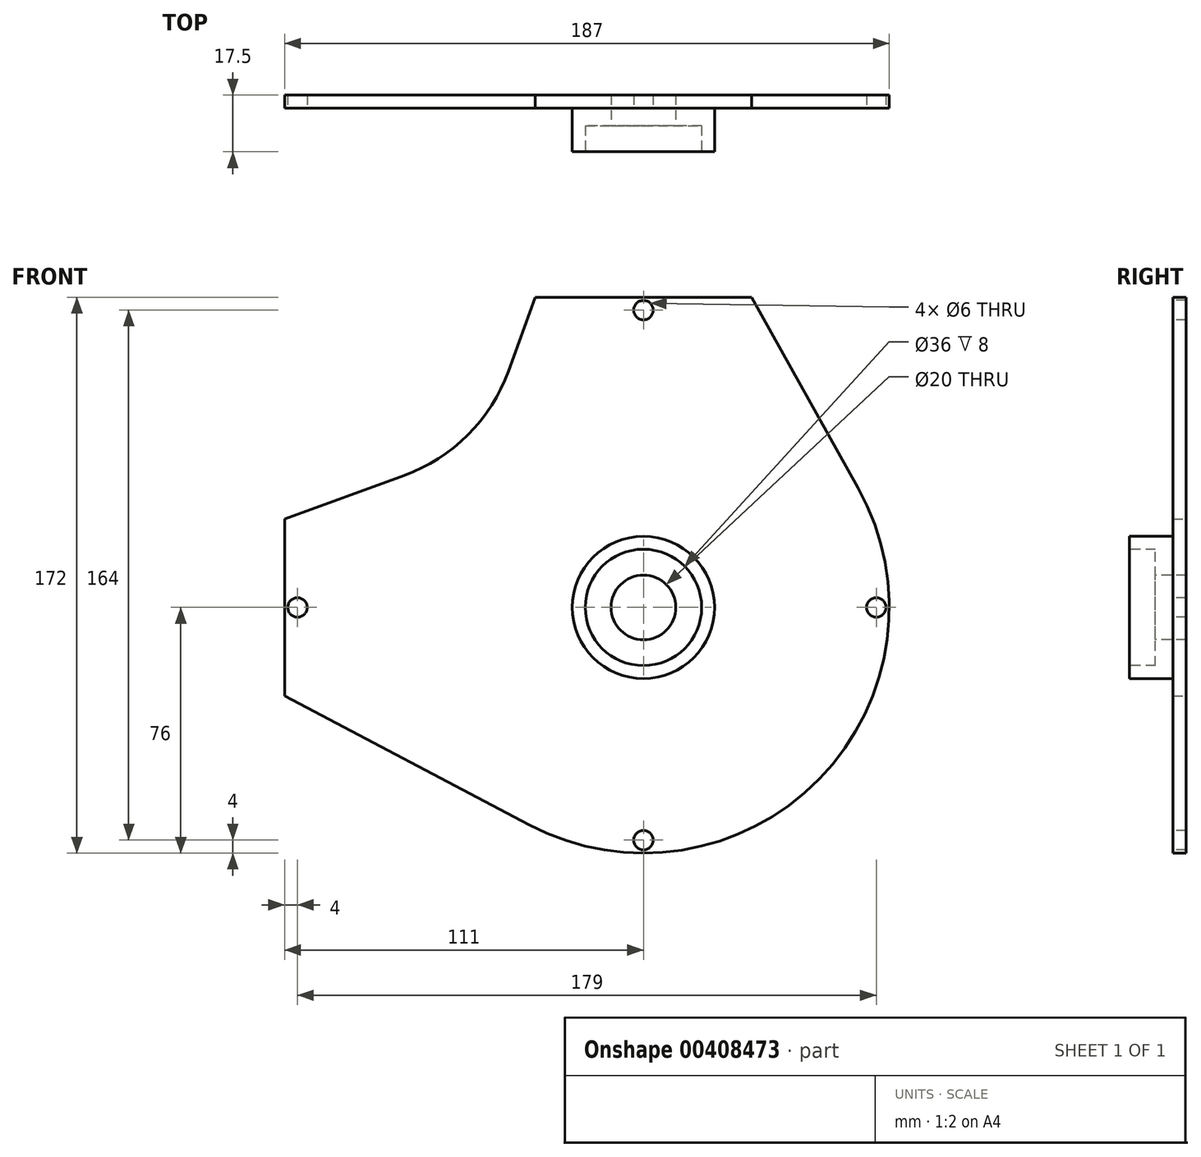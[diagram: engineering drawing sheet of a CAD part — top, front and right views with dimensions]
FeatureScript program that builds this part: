
annotation { "Feature Type Name" : "Feature", "Feature Type Description" : "" }
export const myFeature = defineFeature(function(context is Context, id is Id, definition is map)
    precondition{}
    {
        {
            var Q0;
            Q0=qCreatedBy(makeId("Front.planeOp"),FACE);
            var sketch = newSketch(context, id + "F0", { "sketchPlane" : qUnion([Q0])});
            skLineSegment(sketch, "E0", {"start": v(-33.42, 96) * mm, "end": v(33.42, 96) * mm});
            skLineSegment(sketch, "E1", {"start": v(-111, 27.4) * mm, "end": v(-111, -27.4) * mm});
            skArc(sketch, "E2", {"start": v(66.35, 37.07) * mm, "mid": v(54.39, -53.08) * mm, "end": v(-35.45, -67.23) * mm});
            skLineSegment(sketch, "E3", {"start": v(-111, -27.39) * mm, "end": v(-35.45, -67.23) * mm});
            skLineSegment(sketch, "E4", {"start": v(33.42, 96) * mm, "end": v(66.35, 37.07) * mm});
            skLineSegment(sketch, "E5", {"start": v(-33.42, 96) * mm, "end": v(-41.75, 73.12) * mm});
            skLineSegment(sketch, "E6", {"start": v(-111, 27.39) * mm, "end": v(-74.02, 40.85) * mm});
            skArc(sketch, "E7", {"start": v(-41.75, 73.12) * mm, "mid": v(-54.3, 53.4) * mm, "end": v(-74.02, 40.85) * mm});
            skSolve(sketch);
        }
        {
            var Q0;
            Q0=makeQuery(id+"F0.imprint","IMPRINT",FACE,{"disambiguationData":[TD([[makeQuery(id+"F0.imprint","IMPRINT",EDGE,{"derivedFrom":sQuery(id+"F0.wireOp",EDGE,"E0")}),-1.0]])]});
            extrude(context, id + "F1", {"entities" : qUnion([Q0]), "depth" : 4 * mm});
        }
        {
            var Q0;
            Q0=makeQuery(id+"F1.opExtrude","CAP_FACE",FACE,{"disambiguationData":[OSD([sQuery(id+"F0.wireOp",EDGE,"E0"),sQuery(id+"F0.wireOp",EDGE,"E1"),sQuery(id+"F0.wireOp",EDGE,"E2"),sQuery(id+"F0.wireOp",EDGE,"E3"),sQuery(id+"F0.wireOp",EDGE,"E4"),sQuery(id+"F0.wireOp",EDGE,"E5"),sQuery(id+"F0.wireOp",EDGE,"E6"),sQuery(id+"F0.wireOp",EDGE,"E7")])],"isStart":false});
            var sketch = newSketch(context, id + "F2", { "sketchPlane" : qUnion([Q0])});
            skPoint(sketch, "E8", {"position": v(0, 92) * mm});
            skPoint(sketch, "E9", {"position": v(-107, 0) * mm});
            skPoint(sketch, "E10", {"position": v(0, -72) * mm});
            skPoint(sketch, "E11", {"position": v(72, 0) * mm});
            skSolve(sketch);
        }
        {
            var Q0;
            Q0=sQuery(id+"F2.wireOp",VERTEX,"E8");
            var Q1;
            Q1=sQuery(id+"F2.wireOp",VERTEX,"E9");
            var Q2;
            Q2=sQuery(id+"F2.wireOp",VERTEX,"E10");
            var Q3;
            Q3=sQuery(id+"F2.wireOp",VERTEX,"E11");
            var Q4;
            Q4=makeQuery(id+"F1.opExtrude","SWEPT_BODY",BODY,{"disambiguationData":[OSD([sQuery(id+"F0.wireOp",EDGE,"E0"),sQuery(id+"F0.wireOp",EDGE,"E1"),sQuery(id+"F0.wireOp",EDGE,"E2"),sQuery(id+"F0.wireOp",EDGE,"E3"),sQuery(id+"F0.wireOp",EDGE,"E4"),sQuery(id+"F0.wireOp",EDGE,"E5"),sQuery(id+"F0.wireOp",EDGE,"E6"),sQuery(id+"F0.wireOp",EDGE,"E7")])]});
            hole(context, id + "F3", {"style" : HoleStyle.SIMPLE, "endStyle" : HoleEndStyle.BLIND, "holeDiameter" : 6 * mm, "holeDepth" : 10 * mm, "isTappedThrough" : true, "tappedDepth" : 12 * mm, "tapClearance" : 3, "startFromSketch" : true, "locations" : qUnion([Q0, Q1, Q2, Q3]), "scope" : qUnion([Q4])});
        }
        {
            var Q0;
            Q0=makeQuery(id+"F1.opExtrude","CAP_FACE",FACE,{"disambiguationData":[OSD([sQuery(id+"F0.wireOp",EDGE,"E0"),sQuery(id+"F0.wireOp",EDGE,"E1"),sQuery(id+"F0.wireOp",EDGE,"E2"),sQuery(id+"F0.wireOp",EDGE,"E3"),sQuery(id+"F0.wireOp",EDGE,"E4"),sQuery(id+"F0.wireOp",EDGE,"E5"),sQuery(id+"F0.wireOp",EDGE,"E6"),sQuery(id+"F0.wireOp",EDGE,"E7")])],"isStart":false});
            var sketch = newSketch(context, id + "F4", { "sketchPlane" : qUnion([Q0])});
            skCircle(sketch, "E12", {"center": v(0, 0) * mm, "radius": 22 * mm});
            skSolve(sketch);
        }
        {
            var Q0;
            Q0 = qSketchRegion(id + "F4", true);
            extrude(context, id + "F5", {"entities" : qUnion([Q0]), "operationType" : NewBodyOperationType.ADD, "depth" : 13.5 * mm});
        }
        {
            var Q0;
            Q0=makeQuery(id+"F5.opExtrude","CAP_FACE",FACE,{"disambiguationData":[OSD([sQuery(id+"F4.wireOp",EDGE,"E12")])],"isStart":false});
            var sketch = newSketch(context, id + "F6", { "sketchPlane" : qUnion([Q0])});
            skCircle(sketch, "E13", {"center": v(0, 0) * mm, "radius": 18 * mm});
            skSolve(sketch);
        }
        {
            var Q0;
            Q0 = qSketchRegion(id + "F6", true);
            extrude(context, id + "F7", {"entities" : qUnion([Q0]), "operationType" : NewBodyOperationType.REMOVE, "oppositeDirection" : true, "depth" : 8 * mm});
        }
        {
            var Q0;
            Q0=makeQuery(id+"F7.boolean.opBoolean","COPY",FACE,{"derivedFrom":makeQuery(id+"F7.opExtrude","CAP_FACE",FACE,{"disambiguationData":[OSD([sQuery(id+"F6.wireOp",EDGE,"E13")])],"isStart":false})});
            var sketch = newSketch(context, id + "F8", { "sketchPlane" : qUnion([Q0])});
            skCircle(sketch, "E14", {"center": v(0, 0) * mm, "radius": 10 * mm});
            skSolve(sketch);
        }
        {
            var Q0;
            Q0=makeQuery(id+"F8.imprint","IMPRINT",FACE,{"disambiguationData":[TD([[makeQuery(id+"F8.imprint","IMPRINT",EDGE,{"derivedFrom":sQuery(id+"F8.wireOp",EDGE,"E14")}),1.0]])]});
            extrude(context, id + "F9", {"entities" : qUnion([Q0]), "operationType" : NewBodyOperationType.REMOVE, "oppositeDirection" : true, "depth" : 25 * mm});
        }
    });
